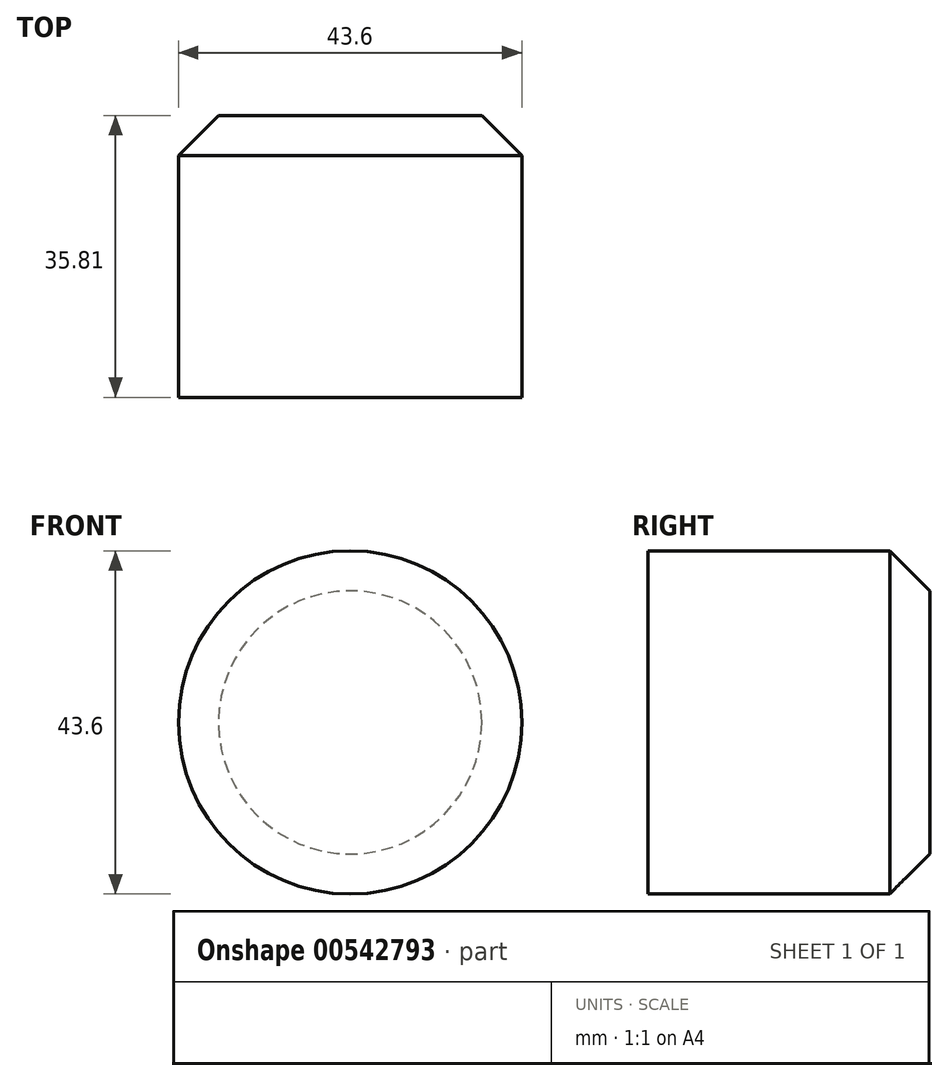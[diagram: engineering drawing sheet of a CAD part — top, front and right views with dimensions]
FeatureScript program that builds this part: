
annotation { "Feature Type Name" : "Feature", "Feature Type Description" : "" }
export const myFeature = defineFeature(function(context is Context, id is Id, definition is map)
    precondition{}
    {
        {
            var Q0;
            Q0=qCreatedBy(makeId("Front.planeOp"),FACE);
            var sketch = newSketch(context, id + "F0", { "sketchPlane" : qUnion([Q0])});
            skCircle(sketch, "E0", {"center": v(-4.77, 9.73) * mm, "radius": 21.8 * mm});
            skSolve(sketch);
        }
        {
            var Q0;
            Q0=makeQuery(id+"F0.imprint","IMPRINT",FACE,{"disambiguationData":[TD([[makeQuery(id+"F0.imprint","IMPRINT",EDGE,{"derivedFrom":sQuery(id+"F0.wireOp",EDGE,"E0")}),1.0]])]});
            extrude(context, id + "F1", {"entities" : qUnion([Q0]), "oppositeDirection" : true, "depth" : 35.81 * mm, "offsetDistance" : 25.4 * mm});
        }
        {
            var Q0;
            Q0=makeQuery(id+"F1.opExtrude","CAP_FACE",FACE,{"disambiguationData":[OSD([sQuery(id+"F0.wireOp",EDGE,"E0")])],"isStart":false});
            chamfer(context, id + "F2", {"entities" : qUnion([Q0]), "width" : 5.08 * mm, "tangentPropagation" : true});
        }
    });
